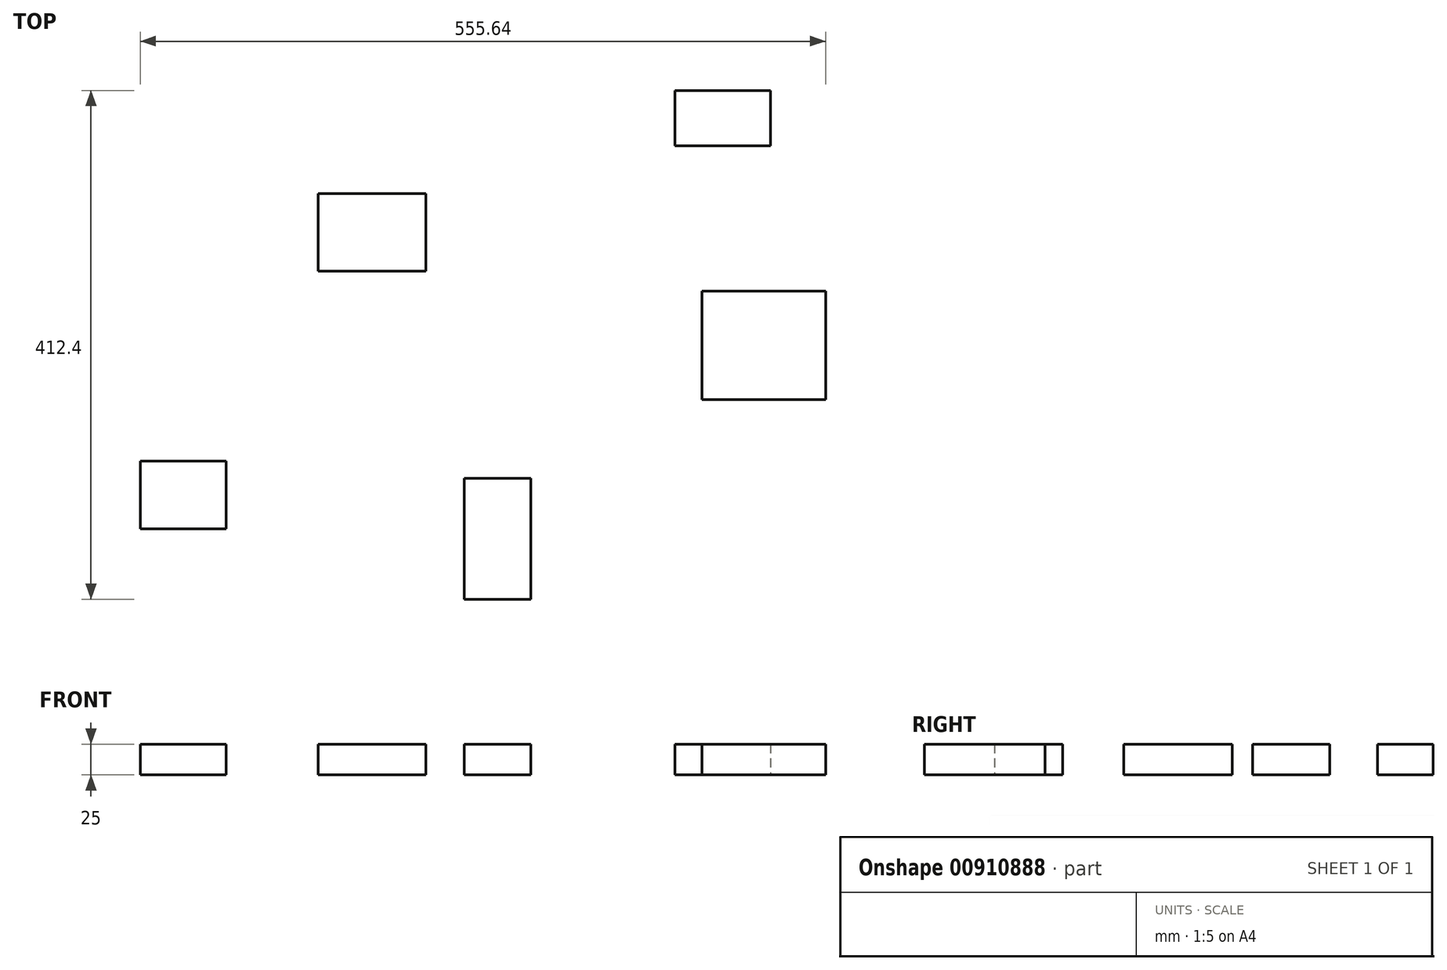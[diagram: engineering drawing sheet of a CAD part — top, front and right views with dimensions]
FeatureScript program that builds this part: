
annotation { "Feature Type Name" : "Feature", "Feature Type Description" : "" }
export const myFeature = defineFeature(function(context is Context, id is Id, definition is map)
    precondition{}
    {
        {
            var Q0;
            Q0=qCreatedBy(makeId("Top.planeOp"),FACE);
            var sketch = newSketch(context, id + "F0", { "sketchPlane" : qUnion([Q0])});
            skLineSegment(sketch, "E0.bottom", {"start": v(-150.27, 79) * mm, "end": v(-63.17, 79) * mm});
            skLineSegment(sketch, "E0.top", {"start": v(-150.27, 16.38) * mm, "end": v(-63.17, 16.38) * mm});
            skLineSegment(sketch, "E0.left", {"start": v(-150.27, 79) * mm, "end": v(-150.27, 16.38) * mm});
            skLineSegment(sketch, "E0.right", {"start": v(-63.17, 79) * mm, "end": v(-63.17, 16.38) * mm});
            skLineSegment(sketch, "E1.bottom", {"start": v(138.66, 162.75) * mm, "end": v(216.22, 162.75) * mm});
            skLineSegment(sketch, "E1.top", {"start": v(138.66, 117.93) * mm, "end": v(216.22, 117.93) * mm});
            skLineSegment(sketch, "E1.left", {"start": v(138.66, 162.75) * mm, "end": v(138.66, 117.93) * mm});
            skLineSegment(sketch, "E1.right", {"start": v(216.22, 162.75) * mm, "end": v(216.22, 117.93) * mm});
            skLineSegment(sketch, "E2.bottom", {"start": v(160.8, 0) * mm, "end": v(261, 0) * mm});
            skLineSegment(sketch, "E2.top", {"start": v(160.8, -87.83) * mm, "end": v(261, -87.83) * mm});
            skLineSegment(sketch, "E2.left", {"start": v(160.8, 0) * mm, "end": v(160.8, -87.83) * mm});
            skLineSegment(sketch, "E2.right", {"start": v(261, 0) * mm, "end": v(261, -87.83) * mm});
            skLineSegment(sketch, "E3.bottom", {"start": v(-32.1, -151.72) * mm, "end": v(21.94, -151.72) * mm});
            skLineSegment(sketch, "E3.top", {"start": v(-32.1, -249.65) * mm, "end": v(21.94, -249.65) * mm});
            skLineSegment(sketch, "E3.left", {"start": v(-32.1, -151.72) * mm, "end": v(-32.1, -249.65) * mm});
            skLineSegment(sketch, "E3.right", {"start": v(21.94, -151.72) * mm, "end": v(21.94, -249.65) * mm});
            skLineSegment(sketch, "E4.bottom", {"start": v(-294.64, -137.65) * mm, "end": v(-225.12, -137.65) * mm});
            skLineSegment(sketch, "E4.top", {"start": v(-294.64, -192.76) * mm, "end": v(-225.12, -192.76) * mm});
            skLineSegment(sketch, "E4.left", {"start": v(-294.64, -137.65) * mm, "end": v(-294.64, -192.76) * mm});
            skLineSegment(sketch, "E4.right", {"start": v(-225.12, -137.65) * mm, "end": v(-225.12, -192.76) * mm});
            skSolve(sketch);
        }
        {
            var Q0;
            Q0=makeQuery(id+"F0.imprint","IMPRINT",FACE,{"disambiguationData":[TD([[makeQuery(id+"F0.imprint","IMPRINT",EDGE,{"derivedFrom":sQuery(id+"F0.wireOp",EDGE,"E0.bottom")}),-1.0]])]});
            var Q1;
            Q1=makeQuery(id+"F0.imprint","IMPRINT",FACE,{"disambiguationData":[TD([[makeQuery(id+"F0.imprint","IMPRINT",EDGE,{"derivedFrom":sQuery(id+"F0.wireOp",EDGE,"E4.bottom")}),-1.0]])]});
            var Q2;
            Q2=makeQuery(id+"F0.imprint","IMPRINT",FACE,{"disambiguationData":[TD([[makeQuery(id+"F0.imprint","IMPRINT",EDGE,{"derivedFrom":sQuery(id+"F0.wireOp",EDGE,"E3.bottom")}),-1.0]])]});
            var Q3;
            Q3=makeQuery(id+"F0.imprint","IMPRINT",FACE,{"disambiguationData":[TD([[makeQuery(id+"F0.imprint","IMPRINT",EDGE,{"derivedFrom":sQuery(id+"F0.wireOp",EDGE,"E2.bottom")}),-1.0]])]});
            var Q4;
            Q4=makeQuery(id+"F0.imprint","IMPRINT",FACE,{"disambiguationData":[TD([[makeQuery(id+"F0.imprint","IMPRINT",EDGE,{"derivedFrom":sQuery(id+"F0.wireOp",EDGE,"E1.bottom")}),-1.0]])]});
            extrude(context, id + "F1", {"entities" : qUnion([Q0, Q1, Q2, Q3, Q4]), "depth" : 25 * mm, "offsetDistance" : 25 * mm});
        }
    });
